# Revit family: FP-Revit18-en-RS6019F3LJ1-Freezer-0-AA-BI-HK-SG-CN-EU-90002454A
name_source: partatom
category: Specialty Equipment
revit_build: Autodesk Revit 2018 (Build: 20170223_1515(x64)
units: mm (PartAtom-declared; Revit-internal decimal feet)

## family parameters
Always vertical = Yes
Cut with Voids When Loaded = Yes
OmniClass Number = 23.40.40.11.11
OmniClass Title = Refrigerators and Freezers
Part Type = Normal
Room Calculation Point = No
Round Connector Dimension = Use Diameter
Shared = No
Work Plane-Based = No

## types (2) — shared parameters
Cavity - Depth (600mm min with services external) = 600 mm
Cavity - Width = 600 mm
Connector Description - Electrical = 230 V, 50 Hz, 10 A circuit
Description = 60cm Integrated Freezer
Manufacturer = Fisher & Paykel Appliances
Material - Body = Fisher & Paykel - Grey
Material - Door Structure = Fisher & Paykel - White
Product - Depth (exl front panel) = 579 mm  [stored 1.89961 ft]
Product - Width = 592 mm  [stored 1.94226 ft]
URL = www.fisherpaykel.com

## per-type parameters (varying)
| type | Connector Description - Water |
| RS6019F2L1 | None |
| RS6019F3LJ1 | min 275 kPa (40 psi) max 827 kPa (120 psi) |

note: column(s) folded — value = type name in every type: Model

note: [stored X ft] marks values corroborated as IEEE doubles in the binary element streams (Revit-internal decimal feet)

## geometry (parser evidence)
native form markers: Sweep x14
no freeform markers — native parametric forms only
